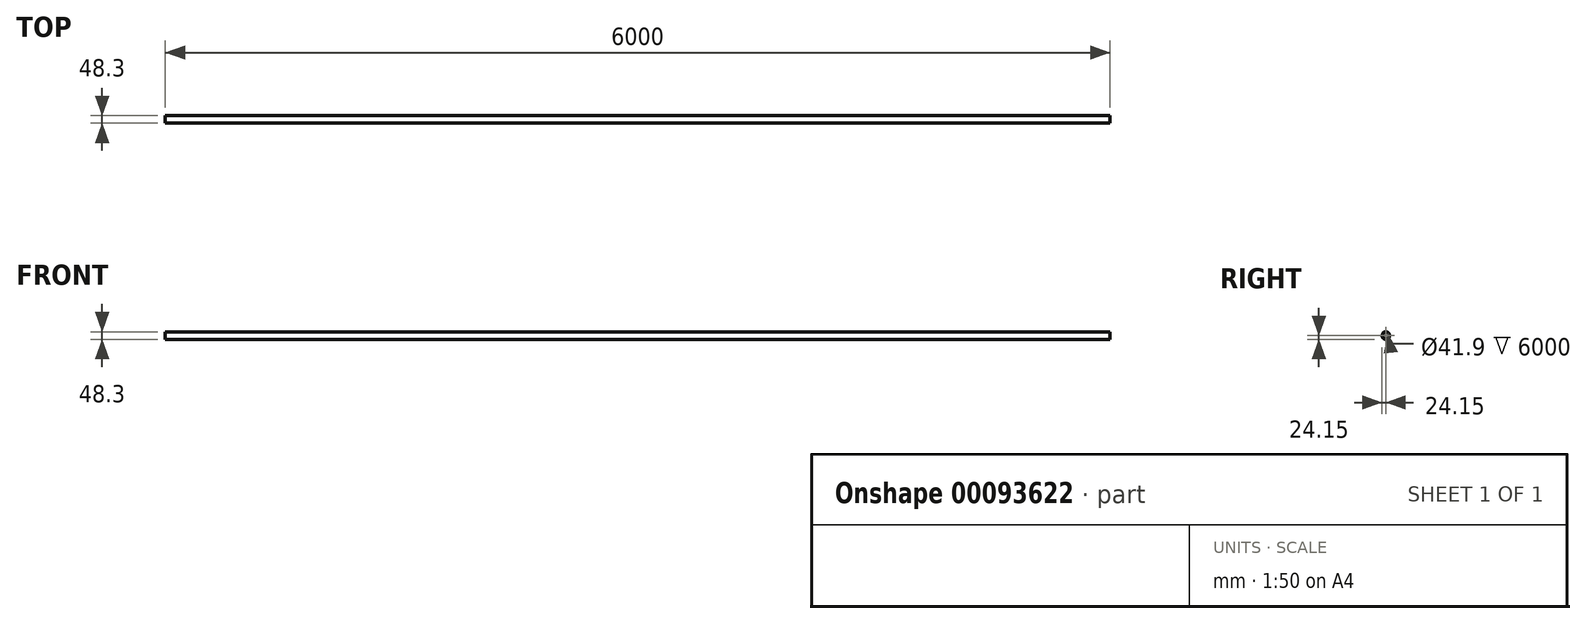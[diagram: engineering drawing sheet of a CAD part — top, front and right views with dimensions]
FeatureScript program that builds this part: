
annotation { "Feature Type Name" : "Feature", "Feature Type Description" : "" }
export const myFeature = defineFeature(function(context is Context, id is Id, definition is map)
    precondition{}
    {
        {
            var Q0;
            Q0=qCreatedBy(makeId("Right.planeOp"),FACE);
            var sketch = newSketch(context, id + "F0", { "sketchPlane" : qUnion([Q0])});
            skCircle(sketch, "E0", {"center": v(0, 0) * mm, "radius": 24.15 * mm});
            skCircle(sketch, "E1", {"center": v(0, 0) * mm, "radius": 20.95 * mm});
            skSolve(sketch);
        }
        {
            var Q0;
            Q0 = qSketchRegion(id + "F0", true);
            extrude(context, id + "F1", {"entities" : qUnion([Q0]), "endBound" : BoundingType.SYMMETRIC, "depth" : 6000 * mm});
        }
    });
